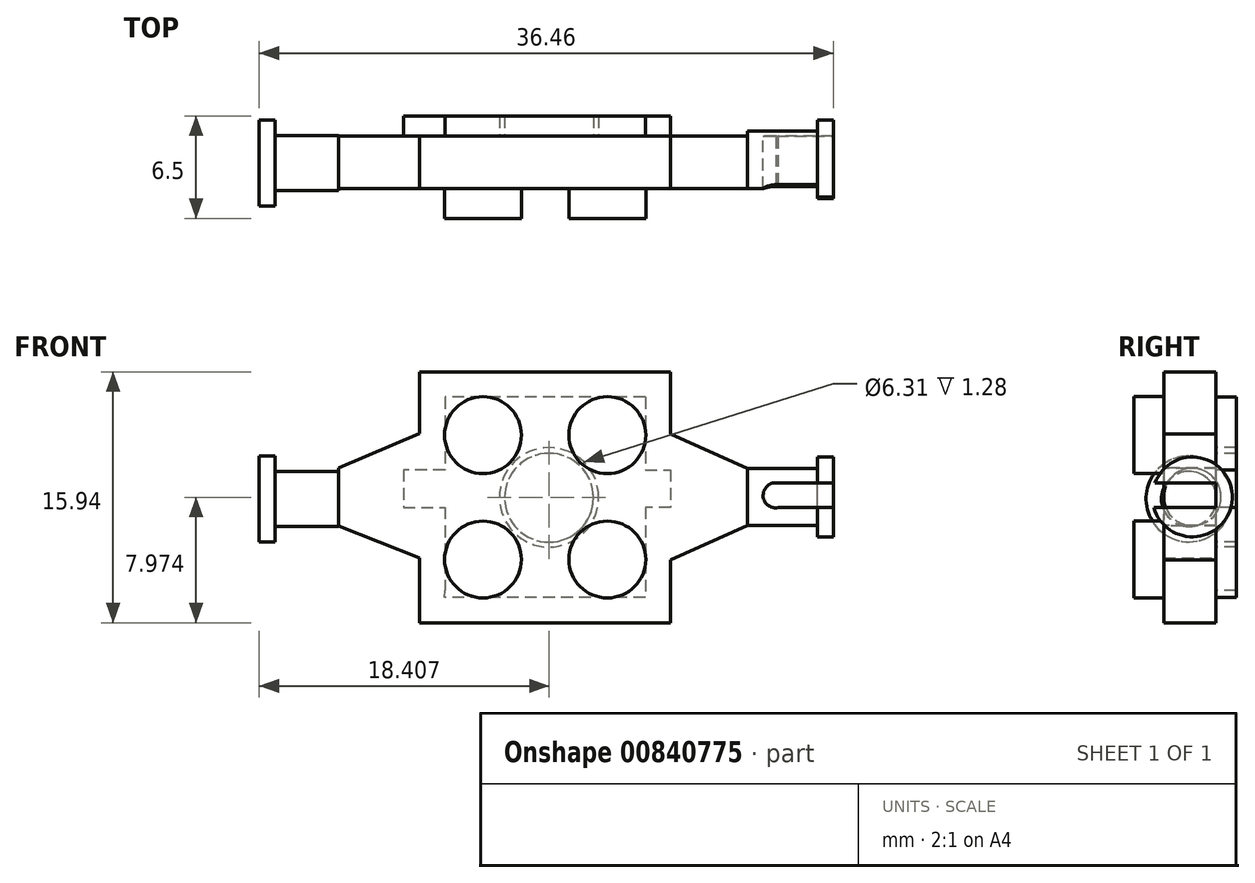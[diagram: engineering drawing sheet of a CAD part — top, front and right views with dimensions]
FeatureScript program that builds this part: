
annotation { "Feature Type Name" : "Feature", "Feature Type Description" : "" }
export const myFeature = defineFeature(function(context is Context, id is Id, definition is map)
    precondition{}
    {
        {
            var Q0;
            Q0=qCreatedBy(makeId("Front.planeOp"),FACE);
            var sketch = newSketch(context, id + "F0", { "sketchPlane" : qUnion([Q0])});
            skLineSegment(sketch, "E0.bottom", {"start": v(-41.3, 42.7) * mm, "end": v(-25.36, 42.7) * mm});
            skLineSegment(sketch, "E0.top", {"start": v(-41.3, 26.75) * mm, "end": v(-25.36, 26.75) * mm});
            skLineSegment(sketch, "E0.left", {"start": v(-41.3, 42.7) * mm, "end": v(-41.3, 26.75) * mm});
            skLineSegment(sketch, "E0.right", {"start": v(-25.36, 42.7) * mm, "end": v(-25.36, 26.75) * mm});
            skSolve(sketch);
        }
        {
            var Q0;
            Q0=makeQuery(id+"F0.imprint","IMPRINT",FACE,{"disambiguationData":[TD([[makeQuery(id+"F0.imprint","IMPRINT",EDGE,{"derivedFrom":sQuery(id+"F0.wireOp",EDGE,"E0.bottom")}),-1.0]])]});
            extrude(context, id + "F1", {"entities" : qUnion([Q0]), "depth" : 3.32 * mm, "offsetDistance" : 25 * mm});
        }
        {
            var Q0;
            Q0=makeQuery(id+"F1.opExtrude","CAP_FACE",FACE,{"disambiguationData":[OSD([sQuery(id+"F0.wireOp",EDGE,"E0.bottom"),sQuery(id+"F0.wireOp",EDGE,"E0.top"),sQuery(id+"F0.wireOp",EDGE,"E0.left"),sQuery(id+"F0.wireOp",EDGE,"E0.right")])],"isStart":false});
            var sketch = newSketch(context, id + "F2", { "sketchPlane" : qUnion([Q0])});
            skCircle(sketch, "E1", {"center": v(-37.28, 38.67) * mm, "radius": 2.44 * mm});
            skCircle(sketch, "E2", {"center": v(-29.38, 38.67) * mm, "radius": 2.44 * mm});
            skCircle(sketch, "E3", {"center": v(-37.28, 30.77) * mm, "radius": 2.44 * mm});
            skCircle(sketch, "E4", {"center": v(-29.38, 30.77) * mm, "radius": 2.44 * mm});
            skLineSegment(sketch, "E5", {"start": v(-26.94, 38.67) * mm, "end": v(-25.36, 38.67) * mm});
            skLineSegment(sketch, "E6", {"start": v(-29.38, 41.11) * mm, "end": v(-29.38, 42.7) * mm});
            skLineSegment(sketch, "E7", {"start": v(-39.72, 38.67) * mm, "end": v(-41.3, 38.67) * mm});
            skLineSegment(sketch, "E8", {"start": v(-37.28, 41.11) * mm, "end": v(-37.28, 42.7) * mm});
            skLineSegment(sketch, "E9", {"start": v(-39.72, 30.77) * mm, "end": v(-41.3, 30.77) * mm});
            skLineSegment(sketch, "E10", {"start": v(-37.28, 28.33) * mm, "end": v(-37.28, 26.75) * mm});
            skLineSegment(sketch, "E11", {"start": v(-29.38, 28.33) * mm, "end": v(-29.38, 26.75) * mm});
            skLineSegment(sketch, "E12", {"start": v(-26.94, 30.77) * mm, "end": v(-25.36, 30.77) * mm});
            skSolve(sketch);
        }
        {
            var Q0;
            Q0=qSketchRegion(id+"F2",true);
            extrude(context, id + "F3", {"entities" : qUnion([Q0]), "operationType" : NewBodyOperationType.ADD, "depth" : 1.9 * mm, "offsetDistance" : 25 * mm});
        }
        {
            var Q0;
            Q0=makeQuery(id+"F1.opExtrude","CAP_FACE",FACE,{"disambiguationData":[OSD([sQuery(id+"F0.wireOp",EDGE,"E0.bottom"),sQuery(id+"F0.wireOp",EDGE,"E0.top"),sQuery(id+"F0.wireOp",EDGE,"E0.left"),sQuery(id+"F0.wireOp",EDGE,"E0.right")])],"isStart":false});
            var sketch = newSketch(context, id + "F4", { "sketchPlane" : qUnion([Q0])});
            skLineSegment(sketch, "E13", {"start": v(-25.36, 38.73) * mm, "end": v(-20.49, 36.54) * mm});
            skLineSegment(sketch, "E14", {"start": v(-20.49, 36.54) * mm, "end": v(-20.49, 32.95) * mm});
            skLineSegment(sketch, "E15", {"start": v(-20.49, 32.95) * mm, "end": v(-25.36, 30.76) * mm});
            skLineSegment(sketch, "E16", {"start": v(-25.36, 30.76) * mm, "end": v(-25.36, 38.73) * mm});
            skSolve(sketch);
        }
        {
            var Q0;
            Q0=qSketchRegion(id+"F4",true);
            extrude(context, id + "F5", {"entities" : qUnion([Q0]), "oppositeDirection" : true, "depth" : 3.32 * mm, "offsetDistance" : 25 * mm});
        }
        {
            var Q0;
            Q0=makeQuery(id+"F5.opExtrude","SWEPT_FACE",FACE,{"disambiguationData":[OSD([sQuery(id+"F4.wireOp",EDGE,"E14")])]});
            var sketch = newSketch(context, id + "F6", { "sketchPlane" : qUnion([Q0])});
            skCircle(sketch, "E17", {"center": v(-1.5, 34.75) * mm, "radius": 1.82 * mm});
            skPoint(sketch, "E17.centerSnap0", {"position": v(0, 34.75) * mm});
            skSolve(sketch);
        }
        {
            var Q0;
            Q0=qSketchRegion(id+"F6",true);
            extrude(context, id + "F7", {"entities" : qUnion([Q0]), "operationType" : NewBodyOperationType.ADD, "depth" : 4.44 * mm, "offsetDistance" : 25 * mm});
        }
        {
            var Q0;
            Q0=makeQuery(id+"F7.opExtrude","CAP_FACE",FACE,{"disambiguationData":[OSD([sQuery(id+"F6.wireOp",EDGE,"E17")])],"isStart":false});
            var sketch = newSketch(context, id + "F8", { "sketchPlane" : qUnion([Q0])});
            skCircle(sketch, "E18", {"center": v(-1.5, 34.75) * mm, "radius": 2.54 * mm});
            skSolve(sketch);
        }
        {
            var Q0;
            Q0=qSketchRegion(id+"F8",true);
            extrude(context, id + "F9", {"entities" : qUnion([Q0]), "operationType" : NewBodyOperationType.ADD, "depth" : 1.02 * mm, "offsetDistance" : 25 * mm});
        }
        {
            var Q0;
            Q0=qCreatedBy(makeId("Front.planeOp"),FACE);
            var sketch = newSketch(context, id + "F10", { "sketchPlane" : qUnion([Q0])});
            skArc(sketch, "E19", {"start": v(-18.64, 35.65) * mm, "mid": v(-19.49, 34.79) * mm, "end": v(-18.52, 34.07) * mm});
            skLineSegment(sketch, "E20", {"start": v(-18.64, 35.65) * mm, "end": v(-15.04, 35.65) * mm});
            skLineSegment(sketch, "E21", {"start": v(-15.04, 35.65) * mm, "end": v(-15.04, 34.07) * mm});
            skLineSegment(sketch, "E22", {"start": v(-15.04, 34.07) * mm, "end": v(-18.52, 34.07) * mm});
            skLineSegment(sketch, "E23", {"start": v(-15.04, 35.65) * mm, "end": v(-14.8, 35.65) * mm});
            skLineSegment(sketch, "E24", {"start": v(-14.8, 35.65) * mm, "end": v(-14.8, 34.07) * mm});
            skLineSegment(sketch, "E25", {"start": v(-14.8, 34.07) * mm, "end": v(-15.04, 34.07) * mm});
            skSolve(sketch);
        }
        {
            var Q0;
            Q0=qSketchRegion(id+"F10",true);
            var Q1;
            Q1=qSketchRegion(id+"FvUQe6Ft84rgAIr_2",true);
            extrude(context, id + "F11", {"entities" : qUnion([Q0, Q1]), "operationType" : NewBodyOperationType.REMOVE, "depth" : 6 * mm, "offsetDistance" : 25 * mm});
        }
        {
            var Q0;
            Q0=makeQuery(id+"F1.opExtrude","CAP_FACE",FACE,{"disambiguationData":[OSD([sQuery(id+"F0.wireOp",EDGE,"E0.bottom"),sQuery(id+"F0.wireOp",EDGE,"E0.top"),sQuery(id+"F0.wireOp",EDGE,"E0.left"),sQuery(id+"F0.wireOp",EDGE,"E0.right")])],"isStart":false});
            var sketch = newSketch(context, id + "F12", { "sketchPlane" : qUnion([Q0])});
            skSolve(sketch);
        }
        {
            var Q0;
            Q0=makeQuery(id+"F12.imprint","IMPRINT",FACE,{"disambiguationData":[TD([[makeQuery(id+"F12.imprint","IMPRINT",EDGE,{"derivedFrom":makeQuery(id+"F1.opExtrude","CAP_EDGE",EDGE,{"disambiguationData":[OSD([sQuery(id+"F0.wireOp",EDGE,"E0.bottom")])],"isStart":false})}),-1.0]])]});
            var sketch = newSketch(context, id + "F13", { "sketchPlane" : qUnion([Q0])});
            skLineSegment(sketch, "E26", {"start": v(-46.45, 32.92) * mm, "end": v(-41.27, 30.85) * mm});
            skLineSegment(sketch, "E27", {"start": v(-41.27, 38.78) * mm, "end": v(-46.45, 36.6) * mm});
            skLineSegment(sketch, "E28", {"start": v(-46.45, 32.92) * mm, "end": v(-46.45, 36.6) * mm});
            skLineSegment(sketch, "E29", {"start": v(-41.27, 38.78) * mm, "end": v(-41.27, 30.85) * mm});
            skSolve(sketch);
        }
        {
            var Q0;
            Q0=qSketchRegion(id+"F13",true);
            extrude(context, id + "F14", {"entities" : qUnion([Q0]), "operationType" : NewBodyOperationType.ADD, "oppositeDirection" : true, "depth" : 3.32 * mm, "offsetDistance" : 25 * mm});
        }
        {
            var Q0;
            Q0=makeQuery(id+"F14.opExtrude","SWEPT_FACE",FACE,{"disambiguationData":[OSD([sQuery(id+"F13.wireOp",EDGE,"E28")])]});
            var sketch = newSketch(context, id + "F15", { "sketchPlane" : qUnion([Q0])});
            skCircle(sketch, "E30", {"center": v(1.71, 34.62) * mm, "radius": 1.75 * mm});
            skPoint(sketch, "E31.center.orphan", {"position": v(1.71, 34.84) * mm});
            skSolve(sketch);
        }
        {
            var Q0;
            Q0=qSketchRegion(id+"F15",true);
            extrude(context, id + "F16", {"entities" : qUnion([Q0]), "operationType" : NewBodyOperationType.ADD, "depth" : 4.02 * mm, "offsetDistance" : 25 * mm});
        }
        {
            var Q0;
            Q0=makeQuery(id+"F16.opExtrude","CAP_FACE",FACE,{"disambiguationData":[OSD([sQuery(id+"F15.wireOp",EDGE,"E30")])],"isStart":false});
            var sketch = newSketch(context, id + "F17", { "sketchPlane" : qUnion([Q0])});
            skCircle(sketch, "E32", {"center": v(1.71, 34.62) * mm, "radius": 2.73 * mm});
            skSolve(sketch);
        }
        {
            var Q0;
            Q0=qSketchRegion(id+"F17",true);
            extrude(context, id + "F18", {"entities" : qUnion([Q0]), "operationType" : NewBodyOperationType.ADD, "depth" : 1.02 * mm, "offsetDistance" : 25 * mm});
        }
        {
            var Q0;
            Q0=makeQuery(id+"F14.boolean.opBoolean","MERGE",FACE,{"derivedFrom":[makeQuery(id+"F1.opExtrude","CAP_FACE",FACE,{"disambiguationData":[OSD([sQuery(id+"F0.wireOp",EDGE,"E0.bottom"),sQuery(id+"F0.wireOp",EDGE,"E0.top"),sQuery(id+"F0.wireOp",EDGE,"E0.left"),sQuery(id+"F0.wireOp",EDGE,"E0.right")])],"isStart":true}),makeQuery(id+"F14.opExtrude","CAP_FACE",FACE,{"disambiguationData":[OSD([sQuery(id+"F13.wireOp",EDGE,"E26"),sQuery(id+"F13.wireOp",EDGE,"E27"),sQuery(id+"F13.wireOp",EDGE,"E28"),sQuery(id+"F13.wireOp",EDGE,"E29")])],"isStart":false})]});
            var sketch = newSketch(context, id + "F19", { "sketchPlane" : qUnion([Q0])});
            skPoint(sketch, "E33.oppositeSnap0", {"position": v(41.3, 28.8) * mm});
            skLineSegment(sketch, "E33.bottom", {"start": v(26.97, 41.08) * mm, "end": v(39.69, 41.08) * mm});
            skLineSegment(sketch, "E33.left", {"start": v(26.97, 41.08) * mm, "end": v(26.97, 36.46) * mm});
            skLineSegment(sketch, "E33.right", {"start": v(39.69, 41.08) * mm, "end": v(39.69, 36.46) * mm});
            skPoint(sketch, "E34.endSnap0", {"position": v(26.97, 35.17) * mm});
            skPoint(sketch, "E34.end.orphan", {"position": v(26.97, 34.95) * mm});
            skPoint(sketch, "E34.start.orphan", {"position": v(25.36, 34.72) * mm});
            skLineSegment(sketch, "E35", {"start": v(26.97, 29.26) * mm, "end": v(26.97, 28.36) * mm});
            skLineSegment(sketch, "E36", {"start": v(26.97, 28.36) * mm, "end": v(39.71, 28.36) * mm});
            skLineSegment(sketch, "E37", {"start": v(39.71, 28.36) * mm, "end": v(39.69, 28.8) * mm});
            skCircle(sketch, "E38", {"center": v(33.08, 34.72) * mm, "radius": 3.15 * mm});
            skCircle(sketch, "E39", {"center": v(33.08, 34.7) * mm, "radius": 2.82 * mm});
            skLineSegment(sketch, "E40", {"start": v(26.97, 36.46) * mm, "end": v(24.32, 36.46) * mm});
            skLineSegment(sketch, "E41", {"start": v(24.32, 36.46) * mm, "end": v(24.32, 34.08) * mm});
            skLineSegment(sketch, "E42", {"start": v(24.32, 34.08) * mm, "end": v(26.97, 34.08) * mm});
            skLineSegment(sketch, "E43", {"start": v(39.69, 36.46) * mm, "end": v(42.34, 36.46) * mm});
            skLineSegment(sketch, "E44", {"start": v(42.34, 36.46) * mm, "end": v(42.34, 34.08) * mm});
            skLineSegment(sketch, "E45", {"start": v(42.34, 34.08) * mm, "end": v(39.69, 34.08) * mm});
            skLineSegment(sketch, "E46.trimOffspring", {"start": v(26.97, 35.17) * mm, "end": v(26.97, 34.95) * mm});
            skLineSegment(sketch, "E47.trimOffspring", {"start": v(26.97, 34.08) * mm, "end": v(26.97, 29.26) * mm});
            skLineSegment(sketch, "E48.trimOffspring", {"start": v(39.69, 34.08) * mm, "end": v(39.69, 28.8) * mm});
            skSolve(sketch);
        }
        {
            var Q0;
            Q0=makeQuery(id+"F19.imprint","IMPRINT",FACE,{"disambiguationData":[TD([[makeQuery(id+"F19.imprint","IMPRINT",EDGE,{"derivedFrom":sQuery(id+"F19.wireOp",EDGE,"E33.bottom")}),-1.0]])]});
            var Q1;
            Q1=makeQuery(id+"F19.imprint","IMPRINT",FACE,{"disambiguationData":[TD([[makeQuery(id+"F19.imprint","IMPRINT",EDGE,{"derivedFrom":sQuery(id+"F19.wireOp",EDGE,"E39")}),1.0]])]});
            extrude(context, id + "F20", {"entities" : qUnion([Q0, Q1]), "operationType" : NewBodyOperationType.ADD, "depth" : 1.28 * mm, "offsetDistance" : 25 * mm});
        }
    });
